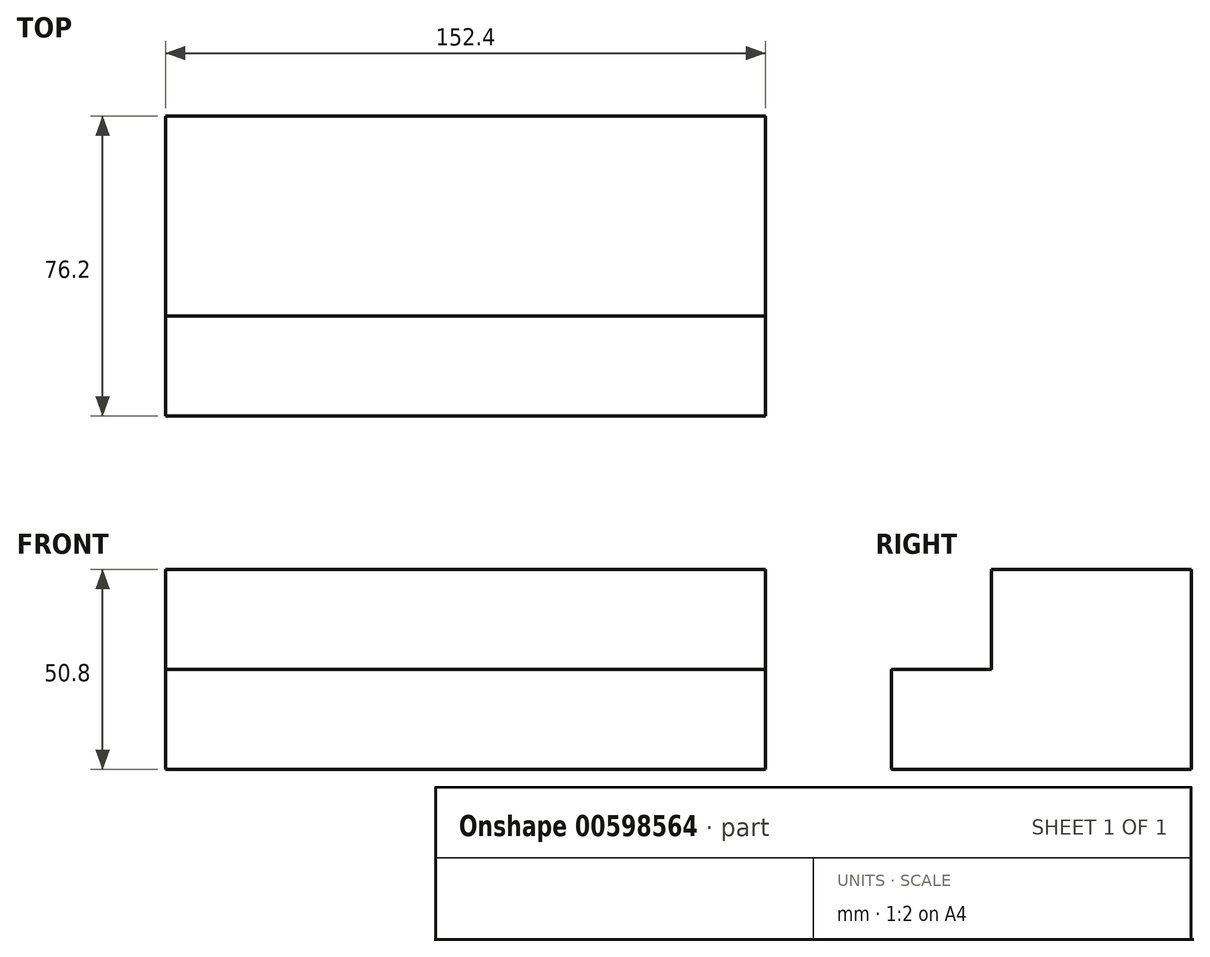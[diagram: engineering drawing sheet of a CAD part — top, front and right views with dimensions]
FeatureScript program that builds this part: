
annotation { "Feature Type Name" : "Feature", "Feature Type Description" : "" }
export const myFeature = defineFeature(function(context is Context, id is Id, definition is map)
    precondition{}
    {
        {
            var Q0;
            Q0=qCreatedBy(makeId("Front.planeOp"),FACE);
            var sketch = newSketch(context, id + "F0", { "sketchPlane" : qUnion([Q0])});
            skLineSegment(sketch, "E0", {"start": v(0, 0) * mm, "end": v(152.4, 0) * mm});
            skLineSegment(sketch, "E1", {"start": v(152.4, 0) * mm, "end": v(152.4, -25.4) * mm});
            skLineSegment(sketch, "E2", {"start": v(152.4, -25.4) * mm, "end": v(0, -25.4) * mm});
            skLineSegment(sketch, "E3", {"start": v(0, -25.4) * mm, "end": v(0, 0) * mm});
            skSolve(sketch);
        }
        {
            var Q0;
            Q0 = qSketchRegion(id + "F0", true);
            extrude(context, id + "F1", {"entities" : qUnion([Q0]), "depth" : 25.4 * mm, "offsetDistance" : 25.4 * mm});
        }
        {
            var Q0;
            Q0=qCreatedBy(makeId("Front.planeOp"),FACE);
            var sketch = newSketch(context, id + "F2", { "sketchPlane" : qUnion([Q0])});
            skLineSegment(sketch, "E4", {"start": v(0, 0) * mm, "end": v(0, 25.4) * mm});
            skLineSegment(sketch, "E5", {"start": v(0, 25.4) * mm, "end": v(152.4, 25.4) * mm});
            skLineSegment(sketch, "E6", {"start": v(152.4, 25.4) * mm, "end": v(152.4, -25.4) * mm});
            skLineSegment(sketch, "E7", {"start": v(152.4, -25.4) * mm, "end": v(0, -25.4) * mm});
            skLineSegment(sketch, "E8", {"start": v(0, -25.4) * mm, "end": v(0, 0) * mm});
            skSolve(sketch);
        }
        {
            var Q0;
            Q0 = qSketchRegion(id + "F2", true);
            extrude(context, id + "F3", {"entities" : qUnion([Q0]), "operationType" : NewBodyOperationType.ADD, "depth" : -50.8 * mm, "offsetDistance" : 25.4 * mm});
        }
    });
